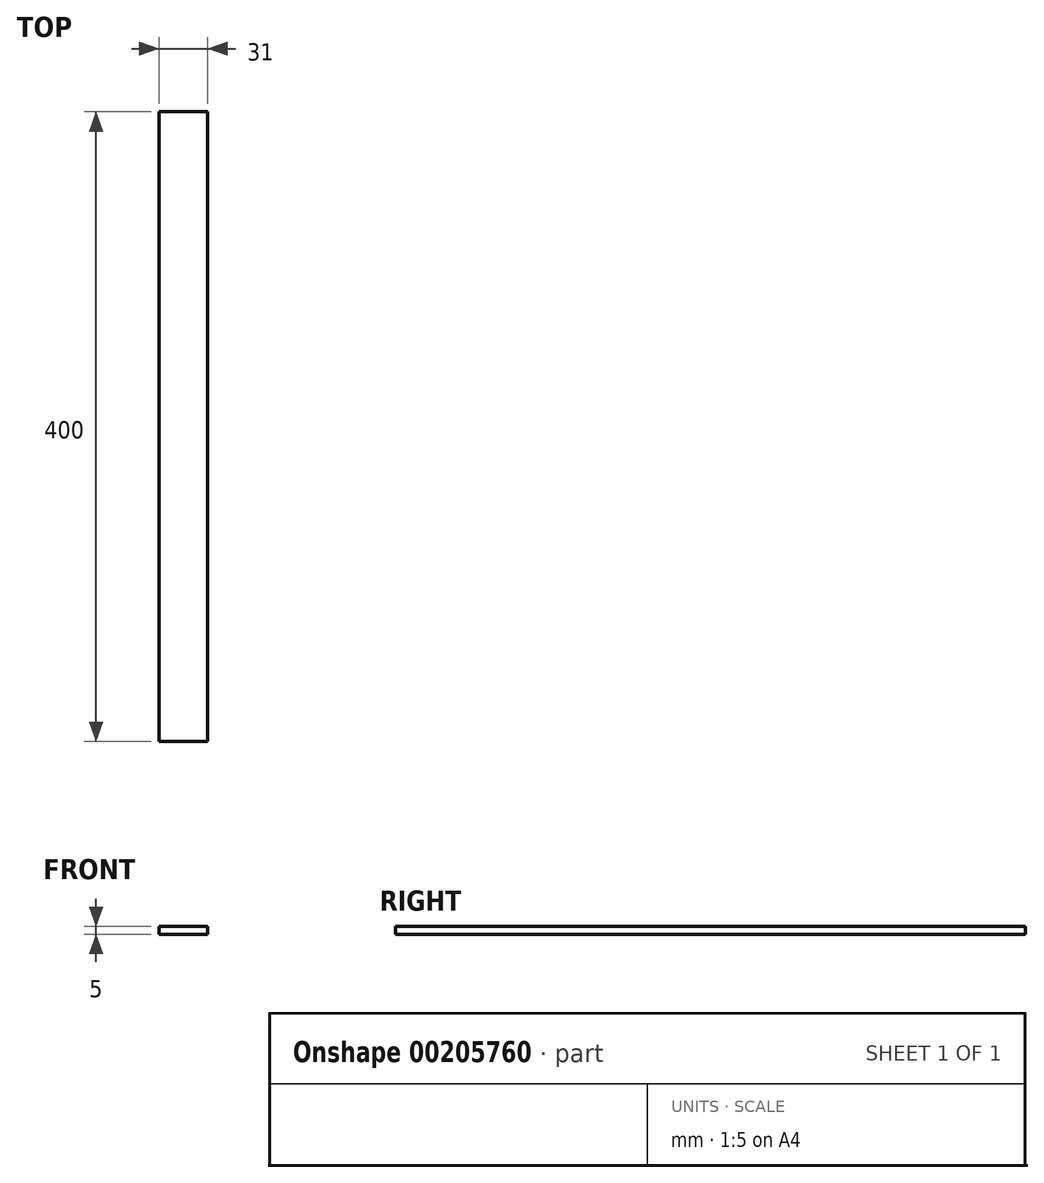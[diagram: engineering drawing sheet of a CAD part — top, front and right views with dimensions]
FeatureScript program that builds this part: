
annotation { "Feature Type Name" : "Feature", "Feature Type Description" : "" }
export const myFeature = defineFeature(function(context is Context, id is Id, definition is map)
    precondition{}
    {
        {
            var Q0;
            Q0=qCreatedBy(makeId("Top.planeOp"),FACE);
            var sketch = newSketch(context, id + "F0", { "sketchPlane" : qUnion([Q0])});
            skLineSegment(sketch, "E0.bottom", {"start": v(-50.15, 366.93) * mm, "end": v(-19.15, 366.93) * mm});
            skLineSegment(sketch, "E0.top", {"start": v(-50.15, -33.07) * mm, "end": v(-19.15, -33.07) * mm});
            skLineSegment(sketch, "E0.left", {"start": v(-50.15, 366.93) * mm, "end": v(-50.15, -33.07) * mm});
            skLineSegment(sketch, "E0.right", {"start": v(-19.15, 366.93) * mm, "end": v(-19.15, -33.07) * mm});
            skSolve(sketch);
        }
        {
            var Q0;
            Q0=makeQuery(id+"F0.imprint","IMPRINT",FACE,{"disambiguationData":[TD([[makeQuery(id+"F0.imprint","IMPRINT",EDGE,{"derivedFrom":sQuery(id+"F0.wireOp",EDGE,"E0.bottom")}),-1.0]])]});
            extrude(context, id + "F1", {"entities" : qUnion([Q0]), "endBound" : BoundingType.SYMMETRIC, "depth" : 5 * mm});
        }
    });
